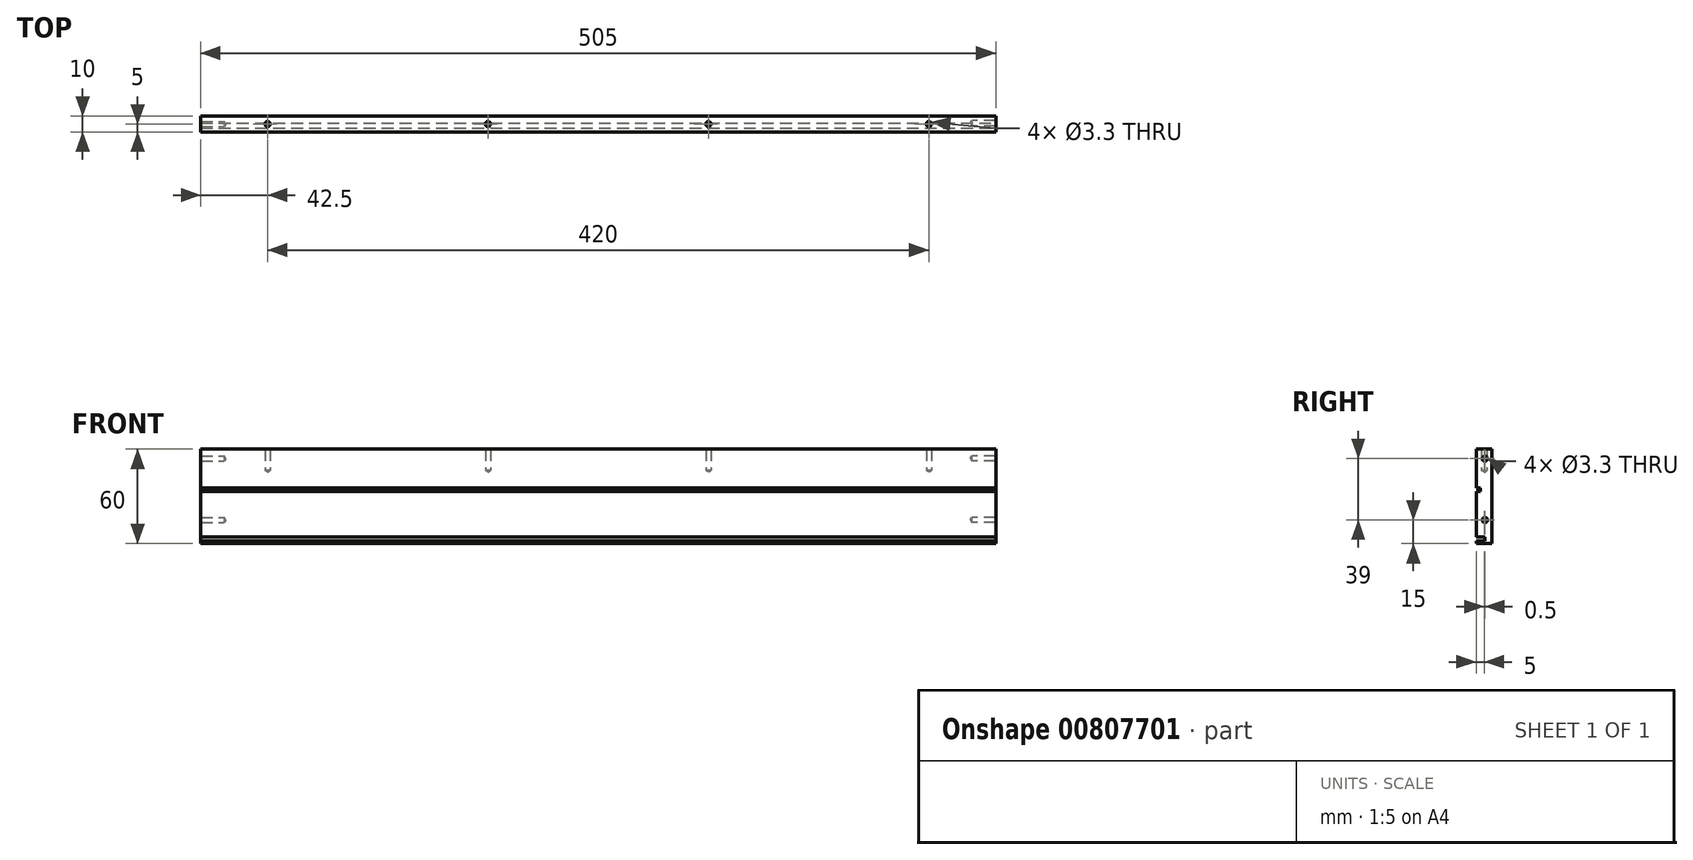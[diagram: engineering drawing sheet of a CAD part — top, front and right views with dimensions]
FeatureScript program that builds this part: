
annotation { "Feature Type Name" : "Feature", "Feature Type Description" : "" }
export const myFeature = defineFeature(function(context is Context, id is Id, definition is map)
    precondition{}
    {
        {
            var Q0;
            Q0=qCreatedBy(makeId("Front.planeOp"),FACE);
            var sketch = newSketch(context, id + "F0", { "sketchPlane" : qUnion([Q0])});
            skLineSegment(sketch, "E0.bottom", {"start": v(252.5, 30) * mm, "end": v(-252.5, 30) * mm});
            skLineSegment(sketch, "E0.top", {"start": v(252.5, -30) * mm, "end": v(-252.5, -30) * mm});
            skLineSegment(sketch, "E0.left", {"start": v(252.5, 30) * mm, "end": v(252.5, -30) * mm});
            skLineSegment(sketch, "E0.right", {"start": v(-252.5, 30) * mm, "end": v(-252.5, -30) * mm});
            skPoint(sketch, "E0.middle", {"position": v(0, 0) * mm});
            skSolve(sketch);
        }
        {
            var Q0;
            Q0 = qSketchRegion(id + "F0", true);
            extrude(context, id + "F1", {"entities" : qUnion([Q0]), "depth" : 10 * mm, "offsetDistance" : 25 * mm});
        }
        {
            var Q0;
            Q0=makeQuery(id+"F1.opExtrude","CAP_FACE",FACE,{"disambiguationData":[OSD([sQuery(id+"F0.wireOp",EDGE,"E0.bottom"),sQuery(id+"F0.wireOp",EDGE,"E0.top"),sQuery(id+"F0.wireOp",EDGE,"E0.left"),sQuery(id+"F0.wireOp",EDGE,"E0.right")])],"isStart":false});
            var sketch = newSketch(context, id + "F2", { "sketchPlane" : qUnion([Q0])});
            skLineSegment(sketch, "E1.bottom", {"start": v(-252.5, -25.9) * mm, "end": v(252.5, -25.9) * mm});
            skLineSegment(sketch, "E1.top", {"start": v(-252.5, -28.2) * mm, "end": v(252.5, -28.2) * mm});
            skLineSegment(sketch, "E1.left", {"start": v(-252.5, -25.9) * mm, "end": v(-252.5, -28.2) * mm});
            skLineSegment(sketch, "E1.right", {"start": v(252.5, -25.9) * mm, "end": v(252.5, -28.2) * mm});
            skSolve(sketch);
        }
        {
            var Q0;
            Q0 = qSketchRegion(id + "F2", true);
            extrude(context, id + "F3", {"entities" : qUnion([Q0]), "operationType" : NewBodyOperationType.REMOVE, "oppositeDirection" : true, "depth" : 5.5 * mm, "offsetDistance" : 25 * mm});
        }
        {
            var Q0;
            {var subQ0=sQuery(id+"F0.wireOp",EDGE,"E0.bottom");var subQ1=sQuery(id+"F0.wireOp",EDGE,"E0.right");var subQ2=sQuery(id+"F0.wireOp",EDGE,"E0.left");Q0=makeQuery(id+"F3.boolean.opBoolean","SPLIT",FACE,{"disambiguationData":[TD([makeQuery(id+"F1.opExtrude","SWEPT_FACE",FACE,{"disambiguationData":[OSD([subQ0])]})])],"derivedFrom":makeQuery(id+"F1.opExtrude","CAP_FACE",FACE,{"disambiguationData":[OSD([subQ0,sQuery(id+"F0.wireOp",EDGE,"E0.top"),subQ2,subQ1])],"isStart":false})});}
            var sketch = newSketch(context, id + "F4", { "sketchPlane" : qUnion([Q0])});
            skLineSegment(sketch, "E2.bottom", {"start": v(-252.5, 5.3) * mm, "end": v(252.5, 5.3) * mm});
            skLineSegment(sketch, "E2.top", {"start": v(-252.5, 3) * mm, "end": v(252.5, 3) * mm});
            skLineSegment(sketch, "E2.left", {"start": v(-252.5, 5.3) * mm, "end": v(-252.5, 3) * mm});
            skLineSegment(sketch, "E2.right", {"start": v(252.5, 5.3) * mm, "end": v(252.5, 3) * mm});
            skSolve(sketch);
        }
        {
            var Q0;
            Q0 = qSketchRegion(id + "F4", true);
            extrude(context, id + "F5", {"entities" : qUnion([Q0]), "operationType" : NewBodyOperationType.REMOVE, "oppositeDirection" : true, "depth" : 2.5 * mm, "offsetDistance" : 25 * mm});
        }
        {
            var Q0;
            Q0=makeQuery(id+"F1.opExtrude","SWEPT_FACE",FACE,{"disambiguationData":[OSD([sQuery(id+"F0.wireOp",EDGE,"E0.bottom")])]});
            var sketch = newSketch(context, id + "F6", { "sketchPlane" : qUnion([Q0])});
            skPoint(sketch, "E3", {"position": v(-70, -5) * mm});
            skPoint(sketch, "E3.positionSnap0", {"position": v(-252.5, -5) * mm});
            skPoint(sketch, "E4", {"position": v(-210, -5) * mm});
            skPoint(sketch, "E5", {"position": v(70, -5) * mm});
            skPoint(sketch, "E6", {"position": v(210, -5) * mm});
            skSolve(sketch);
        }
        {
            var Q0;
            Q0=sQuery(id+"F6.wireOp",VERTEX,"E4");
            var Q1;
            Q1=sQuery(id+"F6.wireOp",VERTEX,"E3");
            var Q2;
            Q2=sQuery(id+"F6.wireOp",VERTEX,"E5");
            var Q3;
            Q3=sQuery(id+"F6.wireOp",VERTEX,"E6");
            var Q4;
            Q4=makeQuery(id+"F1.opExtrude","SWEPT_BODY",BODY,{"disambiguationData":[OSD([sQuery(id+"F0.wireOp",EDGE,"E0.bottom"),sQuery(id+"F0.wireOp",EDGE,"E0.top"),sQuery(id+"F0.wireOp",EDGE,"E0.left"),sQuery(id+"F0.wireOp",EDGE,"E0.right")])]});
            hole(context, id + "F7", {"style" : HoleStyle.SIMPLE, "endStyle" : HoleEndStyle.BLIND, "standardTappedOrClearance" : lookupTablePath({ "standard" : "ISO", "engagement" : "75%", "pitch" : "0.7 mm", "size" : "M4", "type" : "Tapped" }), "standardBlindInLast" : lookupTablePath({ "standard" : "ISO", "engagement" : "75%", "pitch" : "0.7 mm", "size" : "M4", "type" : "Tapped" }), "holeDiameter" : 3.3 * mm, "majorDiameter" : 4 * mm, "showTappedDepth" : true, "holeDepth" : 13.5 * mm, "tappedDepth" : 11.4 * mm, "tapClearance" : 3, "locations" : qUnion([Q0, Q1, Q2, Q3]), "scope" : qUnion([Q4]), "startStyle" : HoleStartStyle.PART});
        }
        {
            var Q0;
            Q0=makeQuery(id+"F1.opExtrude","SWEPT_FACE",FACE,{"disambiguationData":[OSD([sQuery(id+"F0.wireOp",EDGE,"E0.right")])]});
            var sketch = newSketch(context, id + "F8", { "sketchPlane" : qUnion([Q0])});
            skPoint(sketch, "E7", {"position": v(5, -15) * mm});
            skPoint(sketch, "E7.positionSnap0", {"position": v(5, -30) * mm});
            skPoint(sketch, "E8", {"position": v(5, 24) * mm});
            skSolve(sketch);
        }
        {
            var Q0;
            Q0=sQuery(id+"F8.wireOp",VERTEX,"E8");
            var Q1;
            Q1=sQuery(id+"F8.wireOp",VERTEX,"E7");
            var Q2;
            Q2=makeQuery(id+"F1.opExtrude","SWEPT_BODY",BODY,{"disambiguationData":[OSD([sQuery(id+"F0.wireOp",EDGE,"E0.bottom"),sQuery(id+"F0.wireOp",EDGE,"E0.top"),sQuery(id+"F0.wireOp",EDGE,"E0.left"),sQuery(id+"F0.wireOp",EDGE,"E0.right")])]});
            hole(context, id + "F9", {"style" : HoleStyle.SIMPLE, "endStyle" : HoleEndStyle.BLIND, "standardTappedOrClearance" : lookupTablePath({ "standard" : "ISO", "engagement" : "75%", "pitch" : "0.7 mm", "size" : "M4", "type" : "Tapped" }), "standardBlindInLast" : lookupTablePath({ "standard" : "ISO", "engagement" : "75%", "pitch" : "0.7 mm", "size" : "M4", "type" : "Tapped" }), "holeDiameter" : 3.3 * mm, "majorDiameter" : 4 * mm, "showTappedDepth" : true, "holeDepth" : 15 * mm, "tappedDepth" : 12.9 * mm, "tapClearance" : 3, "locations" : qUnion([Q0, Q1]), "scope" : qUnion([Q2]), "startStyle" : HoleStartStyle.PART});
        }
        {
            var Q0;
            Q0=makeQuery(id+"F1.opExtrude","SWEPT_FACE",FACE,{"disambiguationData":[OSD([sQuery(id+"F0.wireOp",EDGE,"E0.left")])]});
            var sketch = newSketch(context, id + "F10", { "sketchPlane" : qUnion([Q0])});
            skPoint(sketch, "E9", {"position": v(-4.5, 30) * mm});
            skPoint(sketch, "E10", {"position": v(-4.5, 24) * mm});
            skPoint(sketch, "E11", {"position": v(-4.5, -15) * mm});
            skSolve(sketch);
        }
        {
            var Q0;
            Q0=sQuery(id+"F10.wireOp",VERTEX,"E11");
            var Q1;
            Q1=sQuery(id+"F10.wireOp",VERTEX,"E10");
            var Q2;
            Q2=makeQuery(id+"F1.opExtrude","SWEPT_BODY",BODY,{"disambiguationData":[OSD([sQuery(id+"F0.wireOp",EDGE,"E0.bottom"),sQuery(id+"F0.wireOp",EDGE,"E0.top"),sQuery(id+"F0.wireOp",EDGE,"E0.left"),sQuery(id+"F0.wireOp",EDGE,"E0.right")])]});
            hole(context, id + "F11", {"style" : HoleStyle.SIMPLE, "endStyle" : HoleEndStyle.BLIND, "standardTappedOrClearance" : lookupTablePath({ "standard" : "ISO", "engagement" : "75%", "pitch" : "0.7 mm", "size" : "M4", "type" : "Tapped" }), "standardBlindInLast" : lookupTablePath({ "standard" : "ISO", "engagement" : "75%", "pitch" : "0.7 mm", "size" : "M4", "type" : "Tapped" }), "holeDiameter" : 3.3 * mm, "majorDiameter" : 4 * mm, "showTappedDepth" : true, "holeDepth" : 15 * mm, "tappedDepth" : 12.9 * mm, "tapClearance" : 3, "locations" : qUnion([Q0, Q1]), "scope" : qUnion([Q2]), "startStyle" : HoleStartStyle.PART});
        }
    });
